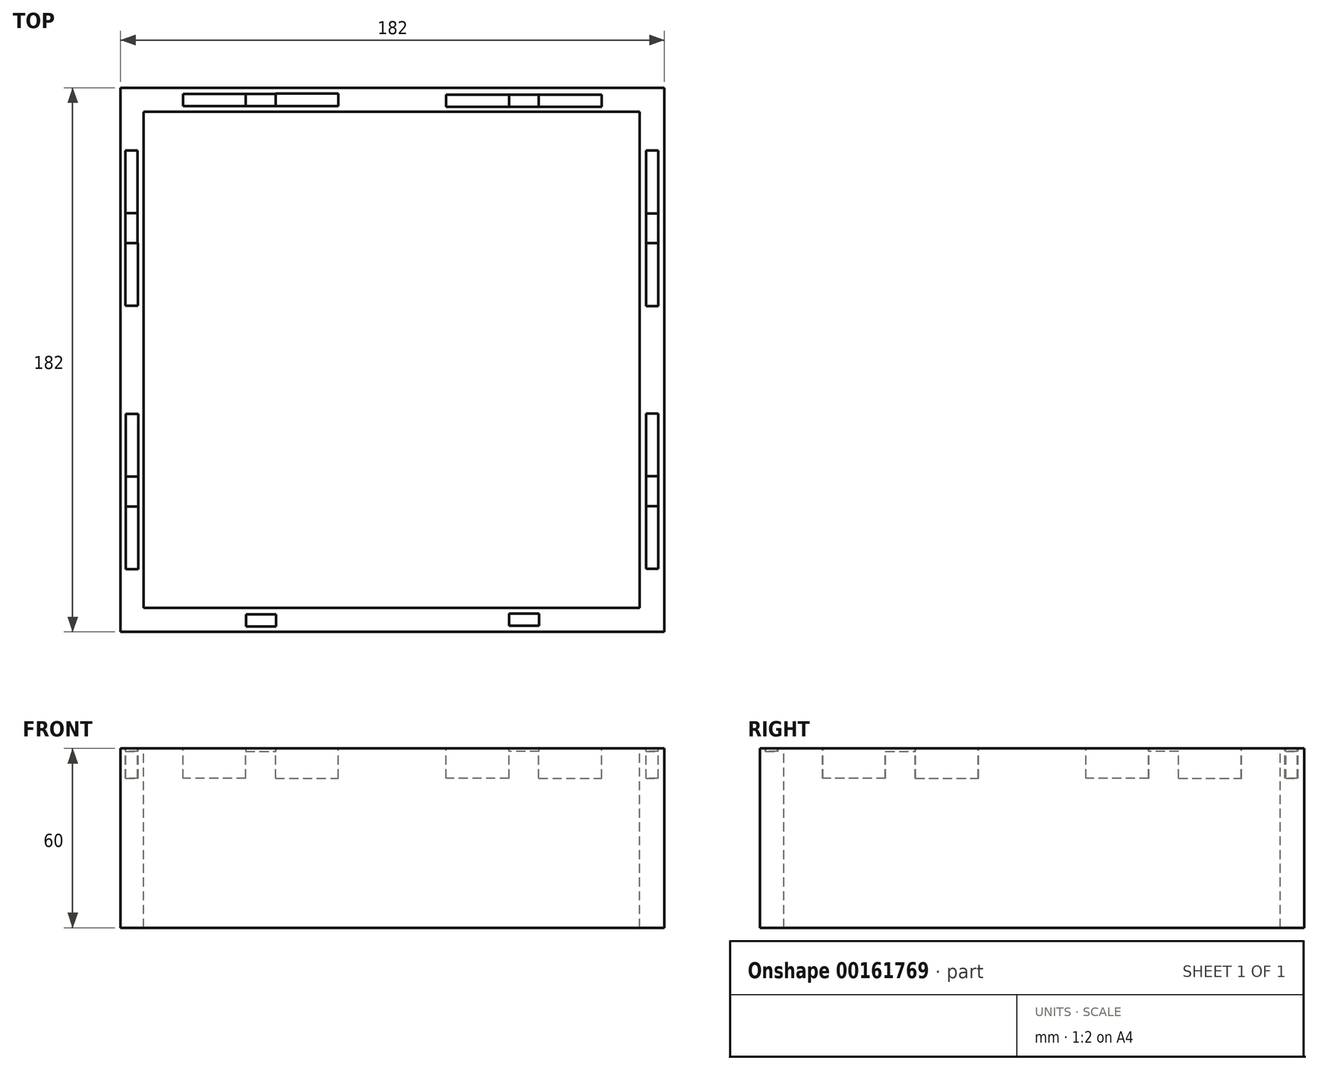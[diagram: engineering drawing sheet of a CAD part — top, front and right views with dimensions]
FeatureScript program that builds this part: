
annotation { "Feature Type Name" : "Feature", "Feature Type Description" : "" }
export const myFeature = defineFeature(function(context is Context, id is Id, definition is map)
    precondition{}
    {
        {
            var Q0;
            Q0=qCreatedBy(makeId("Top.planeOp"),FACE);
            var sketch = newSketch(context, id + "F0", { "sketchPlane" : qUnion([Q0])});
            skLineSegment(sketch, "E0.bottom", {"start": v(-85.04, 91.96) * mm, "end": v(96.96, 91.96) * mm});
            skLineSegment(sketch, "E0.top", {"start": v(-85.04, -90.04) * mm, "end": v(96.96, -90.04) * mm});
            skLineSegment(sketch, "E0.left", {"start": v(-85.04, 91.96) * mm, "end": v(-85.04, -90.04) * mm});
            skLineSegment(sketch, "E0.right", {"start": v(96.96, 91.96) * mm, "end": v(96.96, -90.04) * mm});
            skLineSegment(sketch, "E1.bottom", {"start": v(-77.36, 83.96) * mm, "end": v(88.64, 83.96) * mm});
            skLineSegment(sketch, "E1.top", {"start": v(-77.36, -82.04) * mm, "end": v(88.64, -82.04) * mm});
            skLineSegment(sketch, "E1.left", {"start": v(-77.36, 83.96) * mm, "end": v(-77.36, -82.04) * mm});
            skLineSegment(sketch, "E1.right", {"start": v(88.64, 83.96) * mm, "end": v(88.64, -82.04) * mm});
            skLineSegment(sketch, "E2", {"start": v(60.15, -88.05) * mm, "end": v(60.15, -88.04) * mm});
            skLineSegment(sketch, "E3", {"start": v(60.15, -84.04) * mm, "end": v(60.15, -83.99) * mm});
            skLineSegment(sketch, "E4.bottom", {"start": v(54.96, -83.99) * mm, "end": v(75.96, -83.99) * mm});
            skLineSegment(sketch, "E4.top", {"start": v(54.96, -88.05) * mm, "end": v(75.96, -88.05) * mm});
            skLineSegment(sketch, "E4.left", {"start": v(54.96, -83.99) * mm, "end": v(54.96, -88.05) * mm});
            skLineSegment(sketch, "E4.right", {"start": v(75.96, -83.99) * mm, "end": v(75.96, -88.05) * mm});
            skLineSegment(sketch, "E5.bottom", {"start": v(54.96, -83.99) * mm, "end": v(44.96, -83.99) * mm});
            skLineSegment(sketch, "E5.top", {"start": v(54.96, -88.05) * mm, "end": v(44.96, -88.05) * mm});
            skLineSegment(sketch, "E5.right", {"start": v(44.96, -83.99) * mm, "end": v(44.96, -88.05) * mm});
            skLineSegment(sketch, "E6.bottom", {"start": v(44.96, -83.99) * mm, "end": v(23.96, -83.99) * mm});
            skLineSegment(sketch, "E6.top", {"start": v(44.96, -88.12) * mm, "end": v(23.96, -88.12) * mm});
            skLineSegment(sketch, "E6.left", {"start": v(44.96, -83.99) * mm, "end": v(44.96, -88.12) * mm});
            skLineSegment(sketch, "E6.right", {"start": v(23.96, -83.99) * mm, "end": v(23.96, -88.12) * mm});
            skLineSegment(sketch, "E7", {"start": v(61.36, 83.68) * mm, "end": v(61.36, 83.96) * mm});
            skLineSegment(sketch, "E8", {"start": v(61.36, 89.68) * mm, "end": v(61.36, 89.73) * mm});
            skLineSegment(sketch, "E9.bottom", {"start": v(54.91, 89.73) * mm, "end": v(75.91, 89.73) * mm});
            skLineSegment(sketch, "E9.top", {"start": v(54.91, 85.67) * mm, "end": v(75.91, 85.67) * mm});
            skLineSegment(sketch, "E9.right", {"start": v(75.91, 89.73) * mm, "end": v(75.91, 85.67) * mm});
            skLineSegment(sketch, "E10.bottom", {"start": v(54.91, 89.73) * mm, "end": v(44.91, 89.73) * mm});
            skLineSegment(sketch, "E10.top", {"start": v(54.91, 85.67) * mm, "end": v(44.91, 85.67) * mm});
            skLineSegment(sketch, "E10.left", {"start": v(54.91, 89.73) * mm, "end": v(54.91, 85.67) * mm});
            skLineSegment(sketch, "E11.bottom", {"start": v(44.91, 89.73) * mm, "end": v(23.91, 89.73) * mm});
            skLineSegment(sketch, "E11.top", {"start": v(44.91, 85.6) * mm, "end": v(23.91, 85.6) * mm});
            skLineSegment(sketch, "E11.left", {"start": v(44.91, 89.73) * mm, "end": v(44.91, 85.6) * mm});
            skLineSegment(sketch, "E11.right", {"start": v(23.91, 89.73) * mm, "end": v(23.91, 85.6) * mm});
            skLineSegment(sketch, "E12", {"start": v(-77.35, 55.21) * mm, "end": v(-77.36, 55.21) * mm});
            skLineSegment(sketch, "E13", {"start": v(-83.35, 55.21) * mm, "end": v(-83.4, 55.21) * mm});
            skLineSegment(sketch, "E14.bottom", {"start": v(-83.4, 50.02) * mm, "end": v(-83.4, 71.02) * mm});
            skLineSegment(sketch, "E14.top", {"start": v(-79.33, 50.02) * mm, "end": v(-79.33, 71.02) * mm});
            skLineSegment(sketch, "E14.right", {"start": v(-83.4, 71.02) * mm, "end": v(-79.33, 71.02) * mm});
            skLineSegment(sketch, "E15.bottom", {"start": v(-83.4, 50.02) * mm, "end": v(-83.4, 40.02) * mm});
            skLineSegment(sketch, "E15.top", {"start": v(-79.33, 50.02) * mm, "end": v(-79.33, 40.02) * mm});
            skLineSegment(sketch, "E15.left", {"start": v(-83.4, 50.02) * mm, "end": v(-79.33, 50.02) * mm});
            skLineSegment(sketch, "E16.bottom", {"start": v(-83.4, 40.02) * mm, "end": v(-83.4, 19.02) * mm});
            skLineSegment(sketch, "E16.top", {"start": v(-79.27, 40.02) * mm, "end": v(-79.27, 19.02) * mm});
            skLineSegment(sketch, "E16.left", {"start": v(-83.4, 40.02) * mm, "end": v(-79.27, 40.02) * mm});
            skLineSegment(sketch, "E16.right", {"start": v(-83.4, 19.02) * mm, "end": v(-79.27, 19.02) * mm});
            skLineSegment(sketch, "E17", {"start": v(94.84, 55.15) * mm, "end": v(94.83, 55.15) * mm});
            skLineSegment(sketch, "E18", {"start": v(90.83, 55.15) * mm, "end": v(90.78, 55.15) * mm});
            skLineSegment(sketch, "E19.bottom", {"start": v(90.78, 49.96) * mm, "end": v(90.78, 70.96) * mm});
            skLineSegment(sketch, "E19.top", {"start": v(94.84, 49.96) * mm, "end": v(94.84, 70.96) * mm});
            skLineSegment(sketch, "E19.right", {"start": v(90.78, 70.96) * mm, "end": v(94.84, 70.96) * mm});
            skLineSegment(sketch, "E20.bottom", {"start": v(90.78, 49.96) * mm, "end": v(90.78, 39.96) * mm});
            skLineSegment(sketch, "E20.top", {"start": v(94.84, 49.96) * mm, "end": v(94.84, 39.96) * mm});
            skLineSegment(sketch, "E20.left", {"start": v(90.78, 49.96) * mm, "end": v(94.84, 49.96) * mm});
            skLineSegment(sketch, "E21.bottom", {"start": v(90.78, 39.96) * mm, "end": v(90.78, 18.96) * mm});
            skLineSegment(sketch, "E21.top", {"start": v(94.9, 39.96) * mm, "end": v(94.9, 18.96) * mm});
            skLineSegment(sketch, "E21.left", {"start": v(90.78, 39.96) * mm, "end": v(94.9, 39.96) * mm});
            skLineSegment(sketch, "E21.right", {"start": v(90.78, 18.96) * mm, "end": v(94.9, 18.96) * mm});
            skLineSegment(sketch, "E22", {"start": v(-80.82, -90.04) * mm, "end": v(-80.82, -90.12) * mm});
            skLineSegment(sketch, "E23", {"start": v(-85.22, -53.31) * mm, "end": v(-85.04, -53.31) * mm});
            skLineSegment(sketch, "E24", {"start": v(-79.22, -53.31) * mm, "end": v(-79.17, -53.31) * mm});
            skLineSegment(sketch, "E25.bottom", {"start": v(-79.17, -48.12) * mm, "end": v(-79.17, -69.12) * mm});
            skLineSegment(sketch, "E25.top", {"start": v(-83.24, -48.12) * mm, "end": v(-83.24, -69.12) * mm});
            skLineSegment(sketch, "E25.right", {"start": v(-79.17, -69.12) * mm, "end": v(-83.24, -69.12) * mm});
            skLineSegment(sketch, "E26.bottom", {"start": v(-79.17, -48.12) * mm, "end": v(-79.17, -38.12) * mm});
            skLineSegment(sketch, "E26.top", {"start": v(-83.24, -48.12) * mm, "end": v(-83.24, -38.12) * mm});
            skLineSegment(sketch, "E26.left", {"start": v(-79.17, -48.12) * mm, "end": v(-83.24, -48.12) * mm});
            skLineSegment(sketch, "E27.bottom", {"start": v(-79.17, -38.12) * mm, "end": v(-79.17, -17.12) * mm});
            skLineSegment(sketch, "E27.top", {"start": v(-83.3, -38.12) * mm, "end": v(-83.3, -17.12) * mm});
            skLineSegment(sketch, "E27.left", {"start": v(-79.17, -38.12) * mm, "end": v(-83.3, -38.12) * mm});
            skLineSegment(sketch, "E27.right", {"start": v(-79.17, -17.12) * mm, "end": v(-83.3, -17.12) * mm});
            skLineSegment(sketch, "E28", {"start": v(90.83, -53.18) * mm, "end": v(90.84, -53.18) * mm});
            skLineSegment(sketch, "E29", {"start": v(94.84, -53.18) * mm, "end": v(94.9, -53.18) * mm});
            skLineSegment(sketch, "E30.bottom", {"start": v(94.9, -48) * mm, "end": v(94.9, -69) * mm});
            skLineSegment(sketch, "E30.top", {"start": v(90.83, -48) * mm, "end": v(90.83, -69) * mm});
            skLineSegment(sketch, "E30.right", {"start": v(94.9, -69) * mm, "end": v(90.83, -69) * mm});
            skLineSegment(sketch, "E31.bottom", {"start": v(94.9, -48) * mm, "end": v(94.9, -38) * mm});
            skLineSegment(sketch, "E31.top", {"start": v(90.83, -48) * mm, "end": v(90.83, -38) * mm});
            skLineSegment(sketch, "E31.left", {"start": v(94.9, -48) * mm, "end": v(90.83, -48) * mm});
            skLineSegment(sketch, "E32.bottom", {"start": v(94.9, -38) * mm, "end": v(94.9, -17) * mm});
            skLineSegment(sketch, "E32.top", {"start": v(90.76, -38) * mm, "end": v(90.76, -17) * mm});
            skLineSegment(sketch, "E32.left", {"start": v(94.9, -38) * mm, "end": v(90.76, -38) * mm});
            skLineSegment(sketch, "E32.right", {"start": v(94.9, -17) * mm, "end": v(90.76, -17) * mm});
            skLineSegment(sketch, "E33", {"start": v(-85.04, -86.62) * mm, "end": v(-85.07, -86.62) * mm});
            skLineSegment(sketch, "E34", {"start": v(-48.58, -88.05) * mm, "end": v(-48.58, -88.26) * mm});
            skLineSegment(sketch, "E35.bottom", {"start": v(-43.07, -88.26) * mm, "end": v(-64.07, -88.26) * mm});
            skLineSegment(sketch, "E35.top", {"start": v(-43.07, -84.2) * mm, "end": v(-64.07, -84.2) * mm});
            skLineSegment(sketch, "E35.right", {"start": v(-64.07, -88.26) * mm, "end": v(-64.07, -84.2) * mm});
            skLineSegment(sketch, "E36.bottom", {"start": v(-43.07, -88.26) * mm, "end": v(-33.07, -88.26) * mm});
            skLineSegment(sketch, "E36.top", {"start": v(-43.07, -84.2) * mm, "end": v(-33.07, -84.2) * mm});
            skLineSegment(sketch, "E36.left", {"start": v(-43.07, -88.26) * mm, "end": v(-43.07, -84.2) * mm});
            skLineSegment(sketch, "E37.bottom", {"start": v(-33.07, -88.26) * mm, "end": v(-12.07, -88.26) * mm});
            skLineSegment(sketch, "E37.top", {"start": v(-33.07, -84.13) * mm, "end": v(-12.07, -84.13) * mm});
            skLineSegment(sketch, "E37.left", {"start": v(-33.07, -88.26) * mm, "end": v(-33.07, -84.13) * mm});
            skLineSegment(sketch, "E37.right", {"start": v(-12.07, -88.26) * mm, "end": v(-12.07, -84.13) * mm});
            skLineSegment(sketch, "E38", {"start": v(-85.04, 87.54) * mm, "end": v(-85.17, 87.54) * mm});
            skLineSegment(sketch, "E39", {"start": v(-48.36, 89.96) * mm, "end": v(-48.36, 89.95) * mm});
            skLineSegment(sketch, "E40", {"start": v(-48.36, 85.95) * mm, "end": v(-48.36, 85.9) * mm});
            skLineSegment(sketch, "E41.bottom", {"start": v(-43.17, 85.9) * mm, "end": v(-64.17, 85.9) * mm});
            skLineSegment(sketch, "E41.top", {"start": v(-43.17, 89.96) * mm, "end": v(-64.17, 89.96) * mm});
            skLineSegment(sketch, "E41.right", {"start": v(-64.17, 85.9) * mm, "end": v(-64.17, 89.96) * mm});
            skLineSegment(sketch, "E42.bottom", {"start": v(-43.17, 85.9) * mm, "end": v(-33.17, 85.9) * mm});
            skLineSegment(sketch, "E42.top", {"start": v(-43.17, 89.96) * mm, "end": v(-33.17, 89.96) * mm});
            skLineSegment(sketch, "E42.left", {"start": v(-43.17, 85.9) * mm, "end": v(-43.17, 89.96) * mm});
            skLineSegment(sketch, "E43.bottom", {"start": v(-33.17, 85.9) * mm, "end": v(-12.17, 85.9) * mm});
            skLineSegment(sketch, "E43.top", {"start": v(-33.17, 90.03) * mm, "end": v(-12.17, 90.03) * mm});
            skLineSegment(sketch, "E43.left", {"start": v(-33.17, 85.9) * mm, "end": v(-33.17, 90.03) * mm});
            skLineSegment(sketch, "E43.right", {"start": v(-12.17, 85.9) * mm, "end": v(-12.17, 90.03) * mm});
            skLineSegment(sketch, "E44.trimOffspring", {"start": v(-81.76, 91.96) * mm, "end": v(-81.76, 92.02) * mm});
            skLineSegment(sketch, "E45.trimOffspring", {"start": v(-48.36, 83.96) * mm, "end": v(-48.36, 83.95) * mm});
            skLineSegment(sketch, "E46.trimOffspring", {"start": v(61.36, 85.67) * mm, "end": v(61.36, 85.68) * mm});
            skLineSegment(sketch, "E47.trimOffspring", {"start": v(-79.33, 55.21) * mm, "end": v(-79.35, 55.21) * mm});
            skLineSegment(sketch, "E48.trimOffspring", {"start": v(-85.04, 55.21) * mm, "end": v(-85.35, 55.21) * mm});
            skLineSegment(sketch, "E49.trimOffspring", {"start": v(-77.36, -53.31) * mm, "end": v(-77.22, -53.31) * mm});
            skLineSegment(sketch, "E50.trimOffspring", {"start": v(-83.24, -53.31) * mm, "end": v(-83.22, -53.31) * mm});
            skLineSegment(sketch, "E51.trimOffspring", {"start": v(-48.58, -90.04) * mm, "end": v(-48.58, -90.05) * mm});
            skSolve(sketch);
        }
        {
            var Q0;
            {var subQ78=sQuery(id+"F0.wireOp",EDGE,"E0.right");Q0=makeQuery(id+"F0.imprint","IMPRINT",FACE,{"disambiguationData":[TD([[makeQuery(id+"F0.imprint","IMPRINT",EDGE,{"derivedFrom":subQ78}),-1.0]])]});}
            var Q1;
            {var subQ3=sQuery(id+"F0.wireOp",EDGE,"E16.bottom");Q1=makeQuery(id+"F0.imprint","IMPRINT",FACE,{"disambiguationData":[TD([[makeQuery(id+"F0.imprint","IMPRINT",EDGE,{"derivedFrom":subQ3}),1.0]])]});}
            var Q2;
            {var subQ0=sQuery(id+"F0.wireOp",EDGE,"E15.bottom");Q2=makeQuery(id+"F0.imprint","IMPRINT",FACE,{"disambiguationData":[TD([[makeQuery(id+"F0.imprint","IMPRINT",EDGE,{"derivedFrom":subQ0}),1.0]])]});}
            var Q3;
            {var subQ0=sQuery(id+"F0.wireOp",EDGE,"E14.right");Q3=makeQuery(id+"F0.imprint","IMPRINT",FACE,{"disambiguationData":[TD([[makeQuery(id+"F0.imprint","IMPRINT",EDGE,{"derivedFrom":subQ0}),-1.0]])]});}
            var Q4;
            {var subQ2=sQuery(id+"F0.wireOp",EDGE,"E41.right");Q4=makeQuery(id+"F0.imprint","IMPRINT",FACE,{"disambiguationData":[TD([[makeQuery(id+"F0.imprint","IMPRINT",EDGE,{"derivedFrom":subQ2}),-1.0]])]});}
            var Q5;
            {var subQ0=sQuery(id+"F0.wireOp",EDGE,"E42.bottom");Q5=makeQuery(id+"F0.imprint","IMPRINT",FACE,{"disambiguationData":[TD([[makeQuery(id+"F0.imprint","IMPRINT",EDGE,{"derivedFrom":subQ0}),1.0]])]});}
            var Q6;
            {var subQ3=sQuery(id+"F0.wireOp",EDGE,"E43.bottom");Q6=makeQuery(id+"F0.imprint","IMPRINT",FACE,{"disambiguationData":[TD([[makeQuery(id+"F0.imprint","IMPRINT",EDGE,{"derivedFrom":subQ3}),1.0]])]});}
            var Q7;
            {var subQ3=sQuery(id+"F0.wireOp",EDGE,"E11.bottom");Q7=makeQuery(id+"F0.imprint","IMPRINT",FACE,{"disambiguationData":[TD([[makeQuery(id+"F0.imprint","IMPRINT",EDGE,{"derivedFrom":subQ3}),1.0]])]});}
            var Q8;
            {var subQ0=sQuery(id+"F0.wireOp",EDGE,"E10.bottom");Q8=makeQuery(id+"F0.imprint","IMPRINT",FACE,{"disambiguationData":[TD([[makeQuery(id+"F0.imprint","IMPRINT",EDGE,{"derivedFrom":subQ0}),1.0]])]});}
            var Q9;
            {var subQ0=sQuery(id+"F0.wireOp",EDGE,"E9.right");Q9=makeQuery(id+"F0.imprint","IMPRINT",FACE,{"disambiguationData":[TD([[makeQuery(id+"F0.imprint","IMPRINT",EDGE,{"derivedFrom":subQ0}),-1.0]])]});}
            var Q10;
            {var subQ2=sQuery(id+"F0.wireOp",EDGE,"E19.right");Q10=makeQuery(id+"F0.imprint","IMPRINT",FACE,{"disambiguationData":[TD([[makeQuery(id+"F0.imprint","IMPRINT",EDGE,{"derivedFrom":subQ2}),-1.0]])]});}
            var Q11;
            {var subQ0=sQuery(id+"F0.wireOp",EDGE,"E20.bottom");Q11=makeQuery(id+"F0.imprint","IMPRINT",FACE,{"disambiguationData":[TD([[makeQuery(id+"F0.imprint","IMPRINT",EDGE,{"derivedFrom":subQ0}),1.0]])]});}
            var Q12;
            {var subQ3=sQuery(id+"F0.wireOp",EDGE,"E21.bottom");Q12=makeQuery(id+"F0.imprint","IMPRINT",FACE,{"disambiguationData":[TD([[makeQuery(id+"F0.imprint","IMPRINT",EDGE,{"derivedFrom":subQ3}),1.0]])]});}
            var Q13;
            {var subQ3=sQuery(id+"F0.wireOp",EDGE,"E32.bottom");Q13=makeQuery(id+"F0.imprint","IMPRINT",FACE,{"disambiguationData":[TD([[makeQuery(id+"F0.imprint","IMPRINT",EDGE,{"derivedFrom":subQ3}),1.0]])]});}
            var Q14;
            {var subQ0=sQuery(id+"F0.wireOp",EDGE,"E31.bottom");Q14=makeQuery(id+"F0.imprint","IMPRINT",FACE,{"disambiguationData":[TD([[makeQuery(id+"F0.imprint","IMPRINT",EDGE,{"derivedFrom":subQ0}),1.0]])]});}
            var Q15;
            {var subQ2=sQuery(id+"F0.wireOp",EDGE,"E30.right");Q15=makeQuery(id+"F0.imprint","IMPRINT",FACE,{"disambiguationData":[TD([[makeQuery(id+"F0.imprint","IMPRINT",EDGE,{"derivedFrom":subQ2}),-1.0]])]});}
            var Q16;
            {var subQ2=sQuery(id+"F0.wireOp",EDGE,"E4.right");Q16=makeQuery(id+"F0.imprint","IMPRINT",FACE,{"disambiguationData":[TD([[makeQuery(id+"F0.imprint","IMPRINT",EDGE,{"derivedFrom":subQ2}),-1.0]])]});}
            var Q17;
            {var subQ0=sQuery(id+"F0.wireOp",EDGE,"E5.bottom");Q17=makeQuery(id+"F0.imprint","IMPRINT",FACE,{"disambiguationData":[TD([[makeQuery(id+"F0.imprint","IMPRINT",EDGE,{"derivedFrom":subQ0}),1.0]])]});}
            var Q18;
            {var subQ3=sQuery(id+"F0.wireOp",EDGE,"E6.bottom");Q18=makeQuery(id+"F0.imprint","IMPRINT",FACE,{"disambiguationData":[TD([[makeQuery(id+"F0.imprint","IMPRINT",EDGE,{"derivedFrom":subQ3}),1.0]])]});}
            var Q19;
            {var subQ3=sQuery(id+"F0.wireOp",EDGE,"E37.bottom");Q19=makeQuery(id+"F0.imprint","IMPRINT",FACE,{"disambiguationData":[TD([[makeQuery(id+"F0.imprint","IMPRINT",EDGE,{"derivedFrom":subQ3}),1.0]])]});}
            var Q20;
            {var subQ0=sQuery(id+"F0.wireOp",EDGE,"E36.bottom");Q20=makeQuery(id+"F0.imprint","IMPRINT",FACE,{"disambiguationData":[TD([[makeQuery(id+"F0.imprint","IMPRINT",EDGE,{"derivedFrom":subQ0}),1.0]])]});}
            var Q21;
            Q21=makeQuery(id+"F0.imprint","IMPRINT",FACE,{"disambiguationData":[TD([[makeQuery(id+"F0.imprint","IMPRINT",EDGE,{"derivedFrom":sQuery(id+"F0.wireOp",EDGE,"E35.top")}),1.0]])]});
            var Q22;
            {var subQ0=sQuery(id+"F0.wireOp",EDGE,"E25.right");Q22=makeQuery(id+"F0.imprint","IMPRINT",FACE,{"disambiguationData":[TD([[makeQuery(id+"F0.imprint","IMPRINT",EDGE,{"derivedFrom":subQ0}),-1.0]])]});}
            var Q23;
            {var subQ0=sQuery(id+"F0.wireOp",EDGE,"E26.bottom");Q23=makeQuery(id+"F0.imprint","IMPRINT",FACE,{"disambiguationData":[TD([[makeQuery(id+"F0.imprint","IMPRINT",EDGE,{"derivedFrom":subQ0}),1.0]])]});}
            var Q24;
            {var subQ3=sQuery(id+"F0.wireOp",EDGE,"E27.bottom");Q24=makeQuery(id+"F0.imprint","IMPRINT",FACE,{"disambiguationData":[TD([[makeQuery(id+"F0.imprint","IMPRINT",EDGE,{"derivedFrom":subQ3}),1.0]])]});}
            extrude(context, id + "F1", {"entities" : qUnion([Q0, Q1, Q2, Q3, Q4, Q5, Q6, Q7, Q8, Q9, Q10, Q11, Q12, Q13, Q14, Q15, Q16, Q17, Q18, Q19, Q20, Q21, Q22, Q23, Q24]), "oppositeDirection" : true, "depth" : 60 * mm});
        }
        {
            var Q0;
            {var subQ0=sQuery(id+"F0.wireOp",EDGE,"E14.right");Q0=makeQuery(id+"F0.imprint","IMPRINT",FACE,{"disambiguationData":[TD([[makeQuery(id+"F0.imprint","IMPRINT",EDGE,{"derivedFrom":subQ0}),-1.0]])]});}
            var Q1;
            {var subQ3=sQuery(id+"F0.wireOp",EDGE,"E16.bottom");Q1=makeQuery(id+"F0.imprint","IMPRINT",FACE,{"disambiguationData":[TD([[makeQuery(id+"F0.imprint","IMPRINT",EDGE,{"derivedFrom":subQ3}),1.0]])]});}
            var Q2;
            {var subQ2=sQuery(id+"F0.wireOp",EDGE,"E19.right");Q2=makeQuery(id+"F0.imprint","IMPRINT",FACE,{"disambiguationData":[TD([[makeQuery(id+"F0.imprint","IMPRINT",EDGE,{"derivedFrom":subQ2}),-1.0]])]});}
            var Q3;
            {var subQ3=sQuery(id+"F0.wireOp",EDGE,"E21.bottom");Q3=makeQuery(id+"F0.imprint","IMPRINT",FACE,{"disambiguationData":[TD([[makeQuery(id+"F0.imprint","IMPRINT",EDGE,{"derivedFrom":subQ3}),1.0]])]});}
            var Q4;
            {var subQ3=sQuery(id+"F0.wireOp",EDGE,"E27.bottom");Q4=makeQuery(id+"F0.imprint","IMPRINT",FACE,{"disambiguationData":[TD([[makeQuery(id+"F0.imprint","IMPRINT",EDGE,{"derivedFrom":subQ3}),1.0]])]});}
            var Q5;
            {var subQ0=sQuery(id+"F0.wireOp",EDGE,"E25.right");Q5=makeQuery(id+"F0.imprint","IMPRINT",FACE,{"disambiguationData":[TD([[makeQuery(id+"F0.imprint","IMPRINT",EDGE,{"derivedFrom":subQ0}),-1.0]])]});}
            var Q6;
            {var subQ2=sQuery(id+"F0.wireOp",EDGE,"E30.right");Q6=makeQuery(id+"F0.imprint","IMPRINT",FACE,{"disambiguationData":[TD([[makeQuery(id+"F0.imprint","IMPRINT",EDGE,{"derivedFrom":subQ2}),-1.0]])]});}
            var Q7;
            {var subQ3=sQuery(id+"F0.wireOp",EDGE,"E32.bottom");Q7=makeQuery(id+"F0.imprint","IMPRINT",FACE,{"disambiguationData":[TD([[makeQuery(id+"F0.imprint","IMPRINT",EDGE,{"derivedFrom":subQ3}),1.0]])]});}
            var Q8;
            {var subQ0=sQuery(id+"F0.wireOp",EDGE,"E9.right");Q8=makeQuery(id+"F0.imprint","IMPRINT",FACE,{"disambiguationData":[TD([[makeQuery(id+"F0.imprint","IMPRINT",EDGE,{"derivedFrom":subQ0}),-1.0]])]});}
            var Q9;
            {var subQ3=sQuery(id+"F0.wireOp",EDGE,"E11.bottom");Q9=makeQuery(id+"F0.imprint","IMPRINT",FACE,{"disambiguationData":[TD([[makeQuery(id+"F0.imprint","IMPRINT",EDGE,{"derivedFrom":subQ3}),1.0]])]});}
            var Q10;
            {var subQ3=sQuery(id+"F0.wireOp",EDGE,"E43.bottom");Q10=makeQuery(id+"F0.imprint","IMPRINT",FACE,{"disambiguationData":[TD([[makeQuery(id+"F0.imprint","IMPRINT",EDGE,{"derivedFrom":subQ3}),1.0]])]});}
            var Q11;
            {var subQ2=sQuery(id+"F0.wireOp",EDGE,"E41.right");Q11=makeQuery(id+"F0.imprint","IMPRINT",FACE,{"disambiguationData":[TD([[makeQuery(id+"F0.imprint","IMPRINT",EDGE,{"derivedFrom":subQ2}),-1.0]])]});}
            extrude(context, id + "F2", {"entities" : qUnion([Q0, Q1, Q2, Q3, Q4, Q5, Q6, Q7, Q8, Q9, Q10, Q11]), "operationType" : NewBodyOperationType.REMOVE, "oppositeDirection" : true, "depth" : 10 * mm});
        }
        {
            var Q0;
            {var subQ0=sQuery(id+"F0.wireOp",EDGE,"E15.bottom");Q0=makeQuery(id+"F0.imprint","IMPRINT",FACE,{"disambiguationData":[TD([[makeQuery(id+"F0.imprint","IMPRINT",EDGE,{"derivedFrom":subQ0}),1.0]])]});}
            var Q1;
            {var subQ0=sQuery(id+"F0.wireOp",EDGE,"E26.bottom");Q1=makeQuery(id+"F0.imprint","IMPRINT",FACE,{"disambiguationData":[TD([[makeQuery(id+"F0.imprint","IMPRINT",EDGE,{"derivedFrom":subQ0}),1.0]])]});}
            var Q2;
            {var subQ0=sQuery(id+"F0.wireOp",EDGE,"E31.bottom");Q2=makeQuery(id+"F0.imprint","IMPRINT",FACE,{"disambiguationData":[TD([[makeQuery(id+"F0.imprint","IMPRINT",EDGE,{"derivedFrom":subQ0}),1.0]])]});}
            var Q3;
            {var subQ0=sQuery(id+"F0.wireOp",EDGE,"E20.bottom");Q3=makeQuery(id+"F0.imprint","IMPRINT",FACE,{"disambiguationData":[TD([[makeQuery(id+"F0.imprint","IMPRINT",EDGE,{"derivedFrom":subQ0}),1.0]])]});}
            var Q4;
            {var subQ0=sQuery(id+"F0.wireOp",EDGE,"E10.bottom");Q4=makeQuery(id+"F0.imprint","IMPRINT",FACE,{"disambiguationData":[TD([[makeQuery(id+"F0.imprint","IMPRINT",EDGE,{"derivedFrom":subQ0}),1.0]])]});}
            var Q5;
            {var subQ0=sQuery(id+"F0.wireOp",EDGE,"E42.bottom");Q5=makeQuery(id+"F0.imprint","IMPRINT",FACE,{"disambiguationData":[TD([[makeQuery(id+"F0.imprint","IMPRINT",EDGE,{"derivedFrom":subQ0}),1.0]])]});}
            var Q6;
            {var subQ0=sQuery(id+"F0.wireOp",EDGE,"E36.bottom");Q6=makeQuery(id+"F0.imprint","IMPRINT",FACE,{"disambiguationData":[TD([[makeQuery(id+"F0.imprint","IMPRINT",EDGE,{"derivedFrom":subQ0}),1.0]])]});}
            var Q7;
            {var subQ0=sQuery(id+"F0.wireOp",EDGE,"E5.bottom");Q7=makeQuery(id+"F0.imprint","IMPRINT",FACE,{"disambiguationData":[TD([[makeQuery(id+"F0.imprint","IMPRINT",EDGE,{"derivedFrom":subQ0}),1.0]])]});}
            extrude(context, id + "F3", {"entities" : qUnion([Q0, Q1, Q2, Q3, Q4, Q5, Q6, Q7]), "operationType" : NewBodyOperationType.REMOVE, "oppositeDirection" : true, "depth" : 1 * mm});
        }
    });
